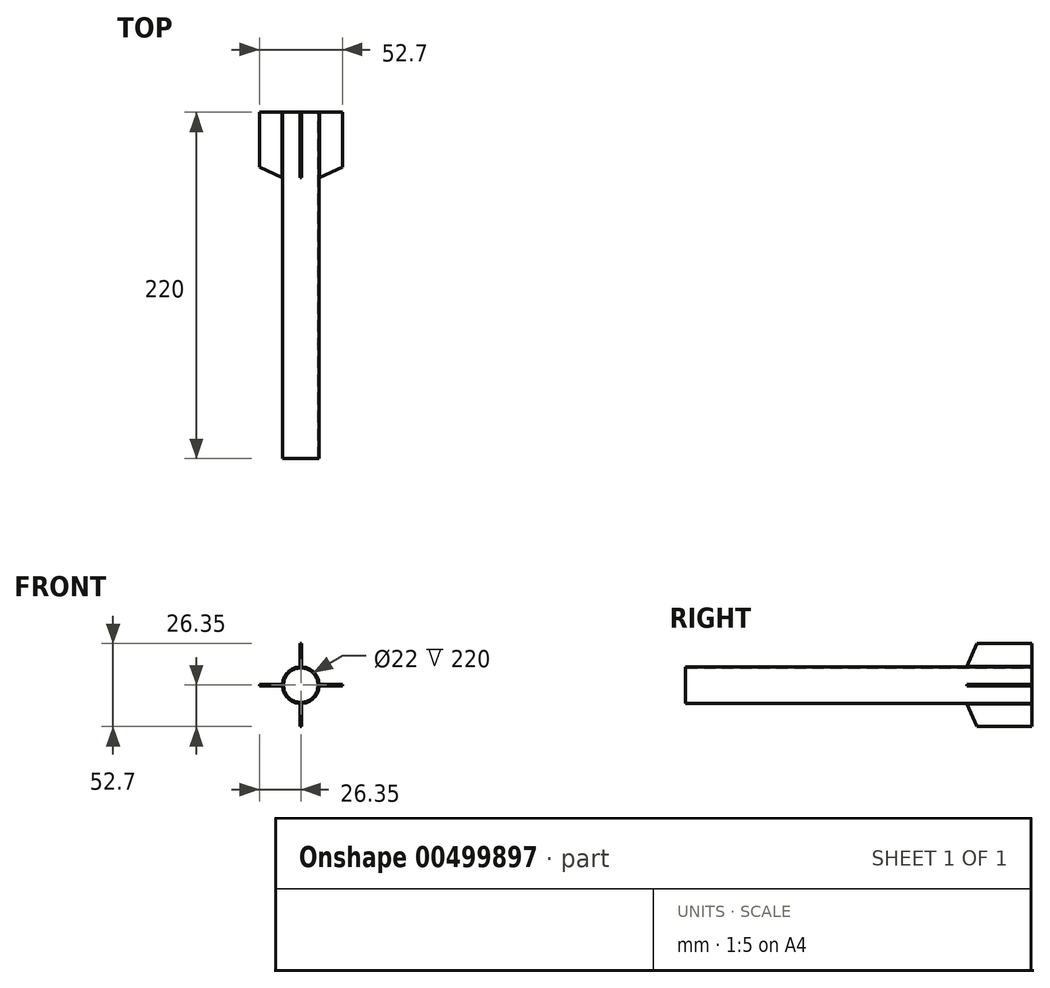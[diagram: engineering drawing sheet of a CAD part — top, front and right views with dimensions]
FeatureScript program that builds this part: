
annotation { "Feature Type Name" : "Feature", "Feature Type Description" : "" }
export const myFeature = defineFeature(function(context is Context, id is Id, definition is map)
    precondition{}
    {
        {
            var Q0;
            Q0=qCreatedBy(makeId("Front.planeOp"),FACE);
            var sketch = newSketch(context, id + "F0", { "sketchPlane" : qUnion([Q0])});
            skCircle(sketch, "E0", {"center": v(0, 0) * mm, "radius": 11 * mm});
            skCircle(sketch, "E1", {"center": v(0, 0) * mm, "radius": 11.65 * mm});
            skSolve(sketch);
        }
        {
            var Q0;
            Q0=makeQuery(id+"F0.imprint","IMPRINT",FACE,{"disambiguationData":[TD([[makeQuery(id+"F0.imprint","IMPRINT",EDGE,{"derivedFrom":sQuery(id+"F0.wireOp",EDGE,"E0")}),-1.0]])]});
            extrude(context, id + "F1", {"entities" : qUnion([Q0]), "depth" : 220 * mm});
        }
        {
            var Q0;
            Q0=qCreatedBy(makeId("Right.planeOp"),FACE);
            var sketch = newSketch(context, id + "F2", { "sketchPlane" : qUnion([Q0])});
            skLineSegment(sketch, "E2", {"start": v(0, 12) * mm, "end": v(-41.3, 12) * mm});
            skLineSegment(sketch, "E3", {"start": v(-41.3, 12) * mm, "end": v(-34.86, 26.35) * mm});
            skLineSegment(sketch, "E4", {"start": v(-34.86, 26.35) * mm, "end": v(0, 26.35) * mm});
            skLineSegment(sketch, "E5", {"start": v(0, 26.35) * mm, "end": v(0, 12) * mm});
            skSolve(sketch);
        }
        {
            var Q0;
            Q0=makeQuery(id+"F2.imprint","IMPRINT",FACE,{"disambiguationData":[TD([[makeQuery(id+"F2.imprint","IMPRINT",EDGE,{"derivedFrom":sQuery(id+"F2.wireOp",EDGE,"E2")}),-1.0]])]});
            extrude(context, id + "F3", {"entities" : qUnion([Q0]), "endBound" : BoundingType.SYMMETRIC, "depth" : 0.8 * mm});
        }
        {
            var Q0;
            Q0=makeQuery(id+"F3.opExtrude","SWEPT_BODY",BODY,{"disambiguationData":[OSD([sQuery(id+"F2.wireOp",EDGE,"E2"),sQuery(id+"F2.wireOp",EDGE,"E3"),sQuery(id+"F2.wireOp",EDGE,"E4"),sQuery(id+"F2.wireOp",EDGE,"E5")])]});
            var Q1;
            Q1=makeQuery(id+"F1.opExtrude","SWEPT_FACE",FACE,{"disambiguationData":[OSD([sQuery(id+"F0.wireOp",EDGE,"E1")])]});
            circularPattern(context, id + "F4", {"operationType" : NewBodyOperationType.ADD, "entities" : qUnion([Q0]), "axis" : qUnion([Q1]), "angle" : 360 * degree, "instanceCount" : 4, "equalSpace" : true});
        }
    });
